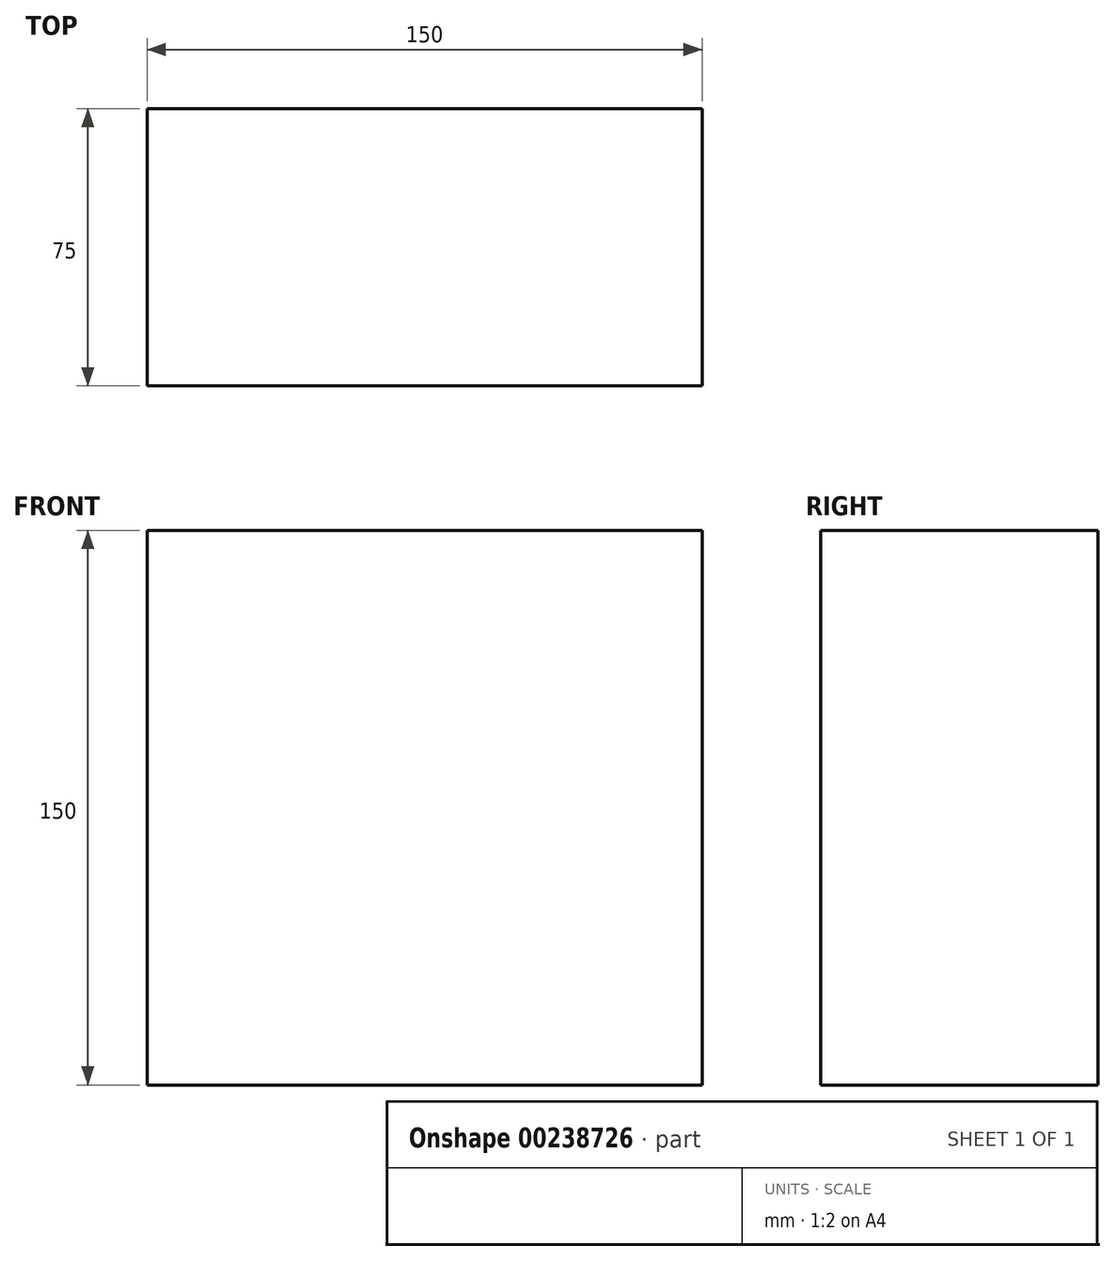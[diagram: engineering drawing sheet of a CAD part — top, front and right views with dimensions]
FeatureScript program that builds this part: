
annotation { "Feature Type Name" : "Feature", "Feature Type Description" : "" }
export const myFeature = defineFeature(function(context is Context, id is Id, definition is map)
    precondition{}
    {
        {
            var Q0;
            Q0=qCreatedBy(makeId("Top.planeOp"),FACE);
            var sketch = newSketch(context, id + "F0", { "sketchPlane" : qUnion([Q0])});
            skLineSegment(sketch, "E0.bottom", {"start": v(0, 0) * mm, "end": v(150, 0) * mm});
            skLineSegment(sketch, "E0.top", {"start": v(0, 75) * mm, "end": v(150, 75) * mm});
            skLineSegment(sketch, "E0.left", {"start": v(0, 0) * mm, "end": v(0, 75) * mm});
            skLineSegment(sketch, "E0.right", {"start": v(150, 0) * mm, "end": v(150, 75) * mm});
            skSolve(sketch);
        }
        {
            var Q0;
            Q0 = qSketchRegion(id + "F0", true);
            extrude(context, id + "F1", {"entities" : qUnion([Q0]), "depth" : 150 * mm});
        }
    });
